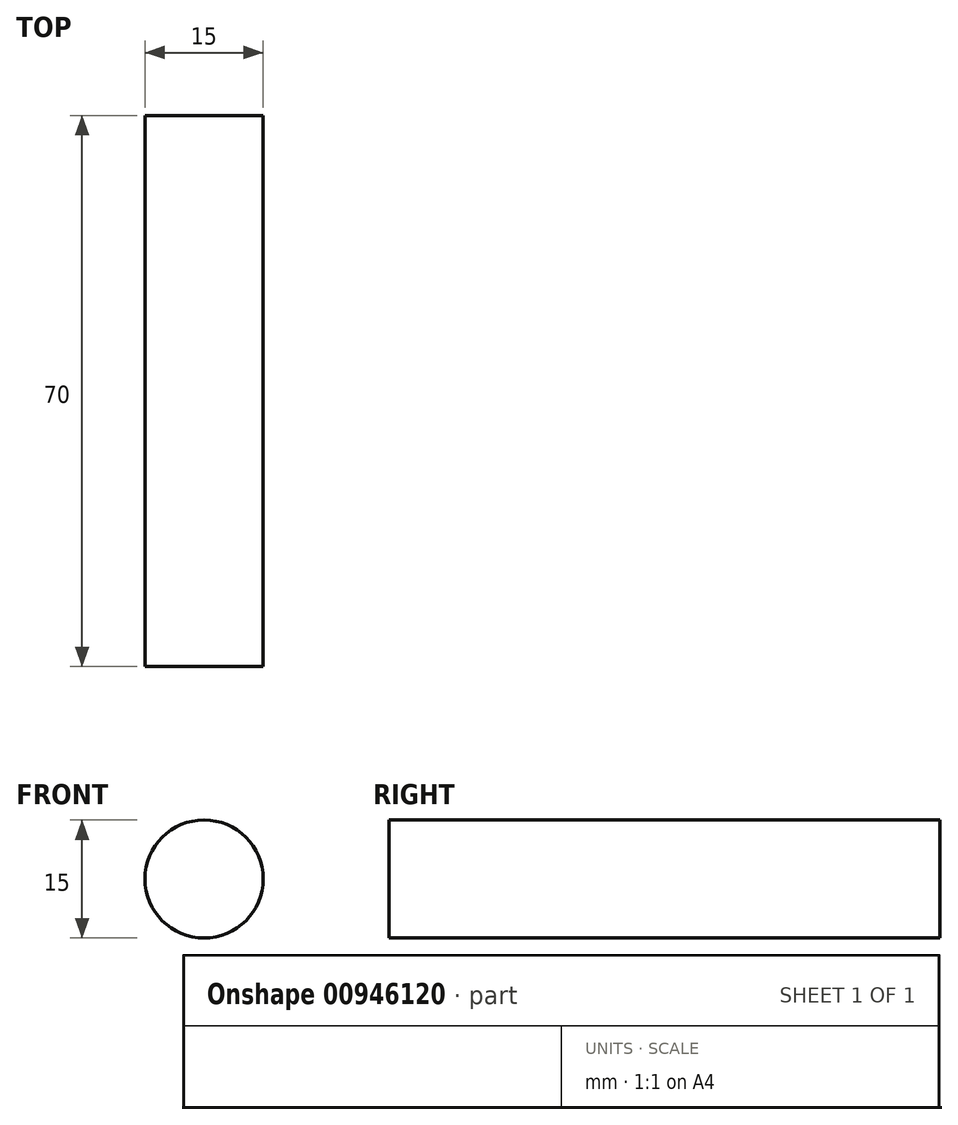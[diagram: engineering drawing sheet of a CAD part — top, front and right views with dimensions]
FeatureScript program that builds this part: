
annotation { "Feature Type Name" : "Feature", "Feature Type Description" : "" }
export const myFeature = defineFeature(function(context is Context, id is Id, definition is map)
    precondition{}
    {
        {
            var Q0;
            Q0=qCreatedBy(makeId("Front.planeOp"),FACE);
            var sketch = newSketch(context, id + "F0", { "sketchPlane" : qUnion([Q0])});
            skCircle(sketch, "E0", {"center": v(0, 0) * mm, "radius": 7.5 * mm});
            skSolve(sketch);
        }
        {
            var Q0;
            Q0=qSketchRegion(id+"F0",true);
            extrude(context, id + "F1", {"entities" : qUnion([Q0]), "endBound" : BoundingType.SYMMETRIC, "depth" : 70 * mm});
        }
    });
